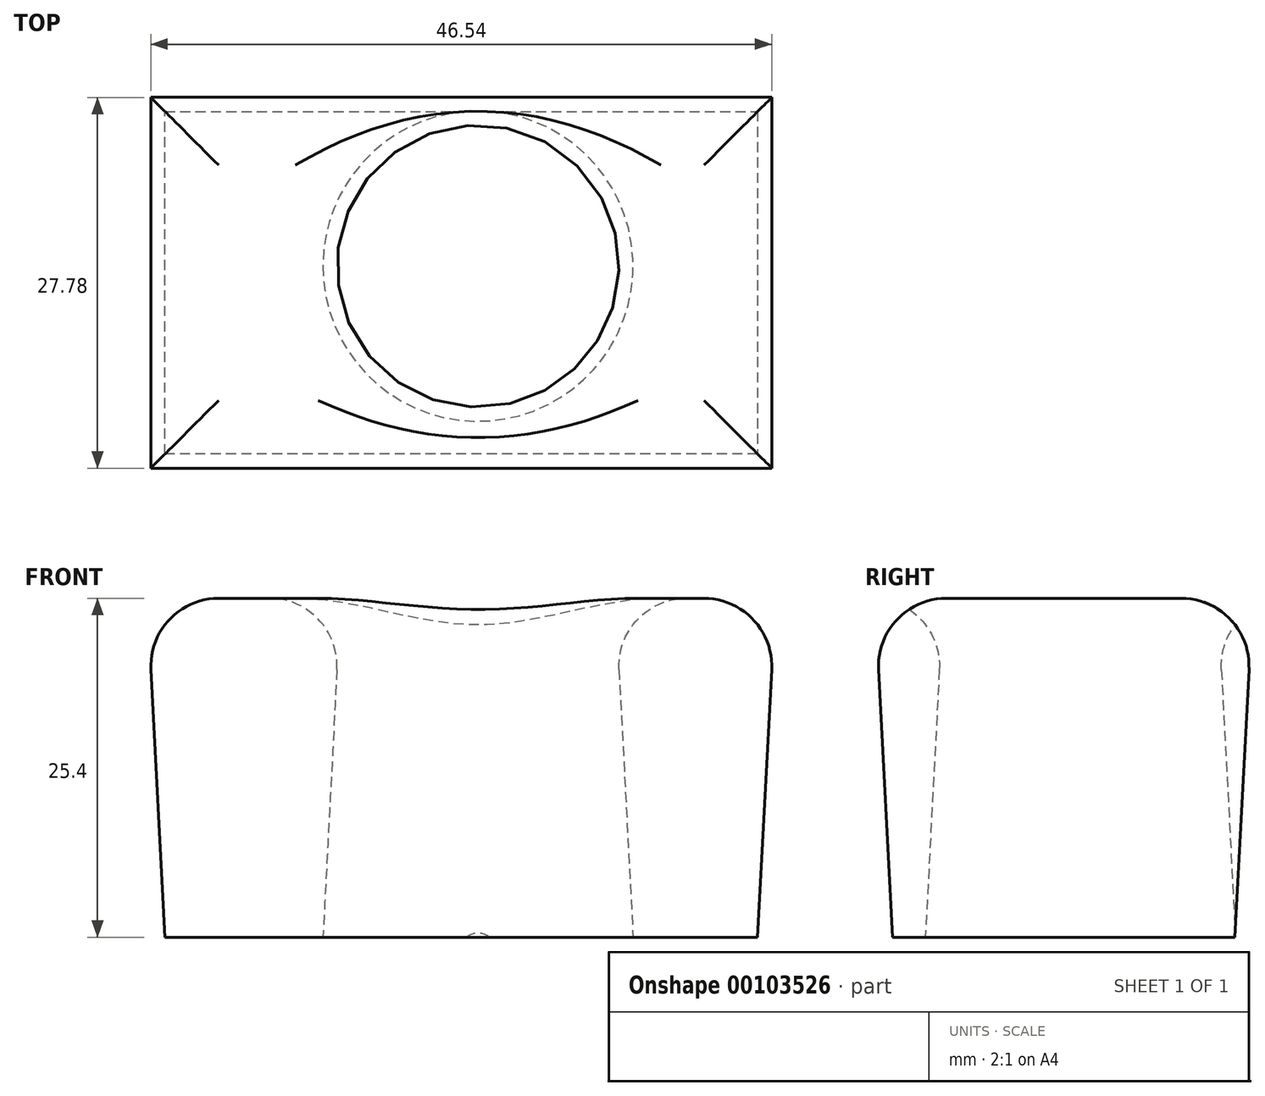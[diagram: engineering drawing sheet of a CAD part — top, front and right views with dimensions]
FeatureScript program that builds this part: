
annotation { "Feature Type Name" : "Feature", "Feature Type Description" : "" }
export const myFeature = defineFeature(function(context is Context, id is Id, definition is map)
    precondition{}
    {
        {
            var Q0;
            Q0=qCreatedBy(makeId("Top.planeOp"),FACE);
            var sketch = newSketch(context, id + "F0", { "sketchPlane" : qUnion([Q0])});
            skLineSegment(sketch, "E0.bottom", {"start": v(-37.28, 2.17) * mm, "end": v(7.15, 2.17) * mm});
            skLineSegment(sketch, "E0.top", {"start": v(-37.28, -23.5) * mm, "end": v(7.15, -23.5) * mm});
            skLineSegment(sketch, "E0.left", {"start": v(-37.28, 2.17) * mm, "end": v(-37.28, -23.5) * mm});
            skLineSegment(sketch, "E0.right", {"start": v(7.15, 2.17) * mm, "end": v(7.15, -23.5) * mm});
            skSolve(sketch);
        }
        {
            var Q0;
            Q0 = qSketchRegion(id + "F0", true);
            extrude(context, id + "F1", {"entities" : qUnion([Q0]), "depth" : 25.4 * mm, "hasDraft" : true, "draftAngle" : 3 * degree});
        }
        {
            var Q0;
            Q0=makeQuery(id+"F1.opExtrude","CAP_FACE",FACE,{"disambiguationData":[OSD([sQuery(id+"F0.wireOp",EDGE,"E0.bottom"),sQuery(id+"F0.wireOp",EDGE,"E0.top"),sQuery(id+"F0.wireOp",EDGE,"E0.left"),sQuery(id+"F0.wireOp",EDGE,"E0.right")])],"isStart":false});
            var sketch = newSketch(context, id + "F2", { "sketchPlane" : qUnion([Q0])});
            skCircle(sketch, "E1", {"center": v(-13.8, -9.42) * mm, "radius": 10.3 * mm});
            skSolve(sketch);
        }
        {
            var Q0;
            Q0 = qSketchRegion(id + "F2", true);
            extrude(context, id + "F3", {"entities" : qUnion([Q0]), "operationType" : NewBodyOperationType.REMOVE, "oppositeDirection" : true, "depth" : 25.4 * mm, "hasDraft" : true, "draftAngle" : 3 * degree});
        }
        {
            var Q0;
            Q0=makeQuery(id+"F1.opExtrude","CAP_EDGE",EDGE,{"disambiguationData":[OSD([sQuery(id+"F0.wireOp",EDGE,"E0.top")])],"isStart":false});
            var Q1;
            Q1=makeQuery(id+"F1.opExtrude","CAP_FACE",FACE,{"disambiguationData":[OSD([sQuery(id+"F0.wireOp",EDGE,"E0.bottom"),sQuery(id+"F0.wireOp",EDGE,"E0.top"),sQuery(id+"F0.wireOp",EDGE,"E0.left"),sQuery(id+"F0.wireOp",EDGE,"E0.right")])],"isStart":false});
            fillet(context, id + "F4", {"entities" : qUnion([Q0, Q1]), "radius" : 5.08 * mm, "tangentPropagation" : true, "allowEdgeOverflow" : false});
        }
    });
